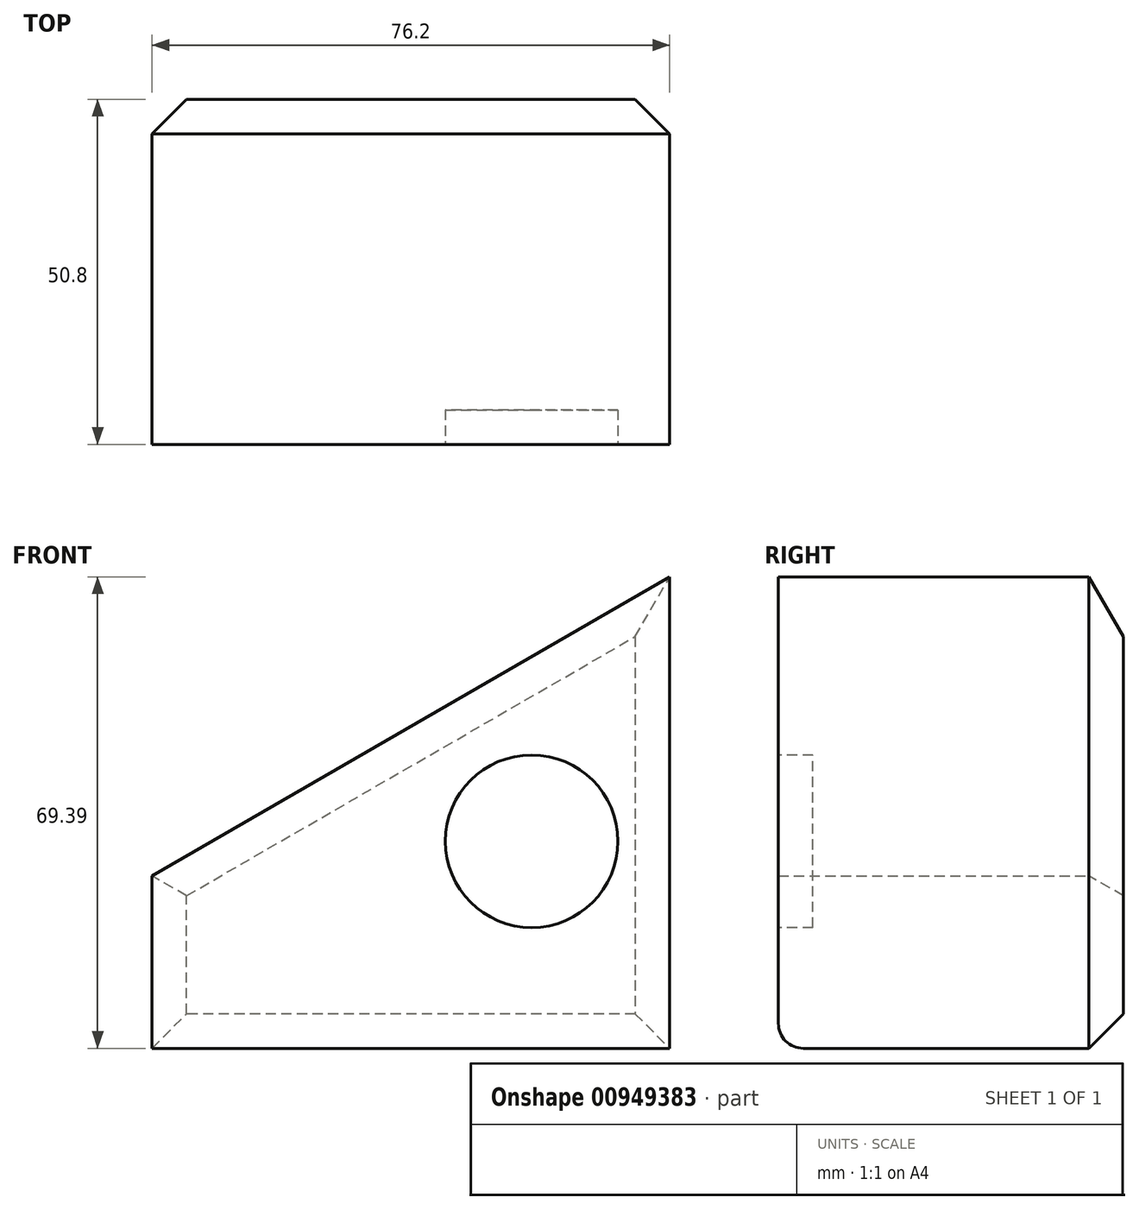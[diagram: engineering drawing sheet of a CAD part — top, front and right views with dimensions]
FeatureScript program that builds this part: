
annotation { "Feature Type Name" : "Feature", "Feature Type Description" : "" }
export const myFeature = defineFeature(function(context is Context, id is Id, definition is map)
    precondition{}
    {
        {
            var Q0;
            Q0=qCreatedBy(makeId("Front.planeOp"),FACE);
            var sketch = newSketch(context, id + "F0", { "sketchPlane" : qUnion([Q0])});
            skLineSegment(sketch, "E0.bottom", {"start": v(0, 0) * mm, "end": v(76.2, 0) * mm});
            skLineSegment(sketch, "E0.top", {"start": v(0, 25.4) * mm, "end": v(76.2, 69.4) * mm});
            skLineSegment(sketch, "E0.left", {"start": v(0, 0) * mm, "end": v(0, 25.4) * mm});
            skLineSegment(sketch, "E0.right", {"start": v(76.2, 0) * mm, "end": v(76.2, 69.4) * mm});
            skSolve(sketch);
        }
        {
            var Q0;
            Q0 = qSketchRegion(id + "F0", true);
            extrude(context, id + "F1", {"entities" : qUnion([Q0]), "depth" : 50.8 * mm, "offsetDistance" : 25.4 * mm});
        }
        {
            var Q0;
            Q0=makeQuery(id+"F1.opExtrude","CAP_FACE",FACE,{"disambiguationData":[OSD([sQuery(id+"F0.wireOp",EDGE,"E0.bottom"),sQuery(id+"F0.wireOp",EDGE,"E0.top"),sQuery(id+"F0.wireOp",EDGE,"E0.left"),sQuery(id+"F0.wireOp",EDGE,"E0.right")])],"isStart":false});
            var sketch = newSketch(context, id + "F2", { "sketchPlane" : qUnion([Q0])});
            skCircle(sketch, "E1", {"center": v(55.88, 30.48) * mm, "radius": 12.7 * mm});
            skSolve(sketch);
        }
        {
            var Q0;
            Q0 = qSketchRegion(id + "F2", true);
            extrude(context, id + "F3", {"entities" : qUnion([Q0]), "operationType" : NewBodyOperationType.REMOVE, "oppositeDirection" : true, "depth" : 5.08 * mm, "offsetDistance" : 25.4 * mm});
        }
        {
            var Q0;
            Q0=makeQuery(id+"F1.opExtrude","CAP_FACE",FACE,{"disambiguationData":[OSD([sQuery(id+"F0.wireOp",EDGE,"E0.bottom"),sQuery(id+"F0.wireOp",EDGE,"E0.top"),sQuery(id+"F0.wireOp",EDGE,"E0.left"),sQuery(id+"F0.wireOp",EDGE,"E0.right")])],"isStart":true});
            chamfer(context, id + "F4", {"entities" : qUnion([Q0]), "width" : 5.08 * mm, "tangentPropagation" : true});
        }
        {
            var Q0;
            Q0=makeQuery(id+"F1.opExtrude","CAP_EDGE",EDGE,{"disambiguationData":[OSD([sQuery(id+"F0.wireOp",EDGE,"E0.bottom")])],"isStart":false});
            fillet(context, id + "F5", {"entities" : qUnion([Q0]), "radius" : 3.68 * mm, "tangentPropagation" : true, "allowEdgeOverflow" : false});
        }
    });
